FCSTD DOCUMENT  (FreeCAD 0.18R16161 (Git))
Label: fixator02
License: All rights reserved
LicenseURL: http://en.wikipedia.org/wiki/All_rights_reserved
objects: Sketcher::SketchObject×1
note: 1 computed .brp shape members not serialized (recipe doc carries the construction recipe); baked Part::Feature solids carry a one-line shape summary decoded from their .brp

FEATURE [Sketcher::SketchObject] Sketch
  sketch-geometry (6):
    g0: Circle CenterX=-7.5 CenterY=0 CenterZ=0 NormalX=0 NormalY=0 NormalZ=1 AngleXU=0 Radius=2.5
    g1: Circle CenterX=2.5 CenterY=0 CenterZ=0 NormalX=0 NormalY=0 NormalZ=1 AngleXU=0 Radius=2.5
    g2: LineSegment StartX=0 StartY=0 StartZ=0 EndX=-5 EndY=0 EndZ=0
    g3: LineSegment StartX=-7.5 StartY=2.5 StartZ=0 EndX=2.5 EndY=2.5 EndZ=0
    g4: LineSegment StartX=-7.5 StartY=-2.5 StartZ=0 EndX=-7.5 EndY=2.5 EndZ=0
    g5: LineSegment StartX=-7.5 StartY=-2.5 StartZ=0 EndX=2.5 EndY=-2.5 EndZ=0
  constraints (19):
    c: PointOnObject(g0,g-1)
    c: PointOnObject(g1,g-1)
    c: Diameter(g0) = 5
    c: Equal(g1,g0)
    c: PointOnObject(g-1,g1)
    c: Horizontal(g2)
    c: DistanceX(g2,g2) = 5
    c: Coincident(g2,g-1)
    c: PointOnObject(g2,g0)
    c: Horizontal(g3)
    c: DistanceX(g3,g3) = 10
    c: Vertical(g4)
    c: DistanceY(g4,g4) = 5
    c: PointOnObject(g0,g4)
    c: PointOnObject(g4,g0)
    c: Coincident(g3,g4)
    c: Coincident(g5,g4)
    c: Equal(g5,g3)
    c: Horizontal(g5)
